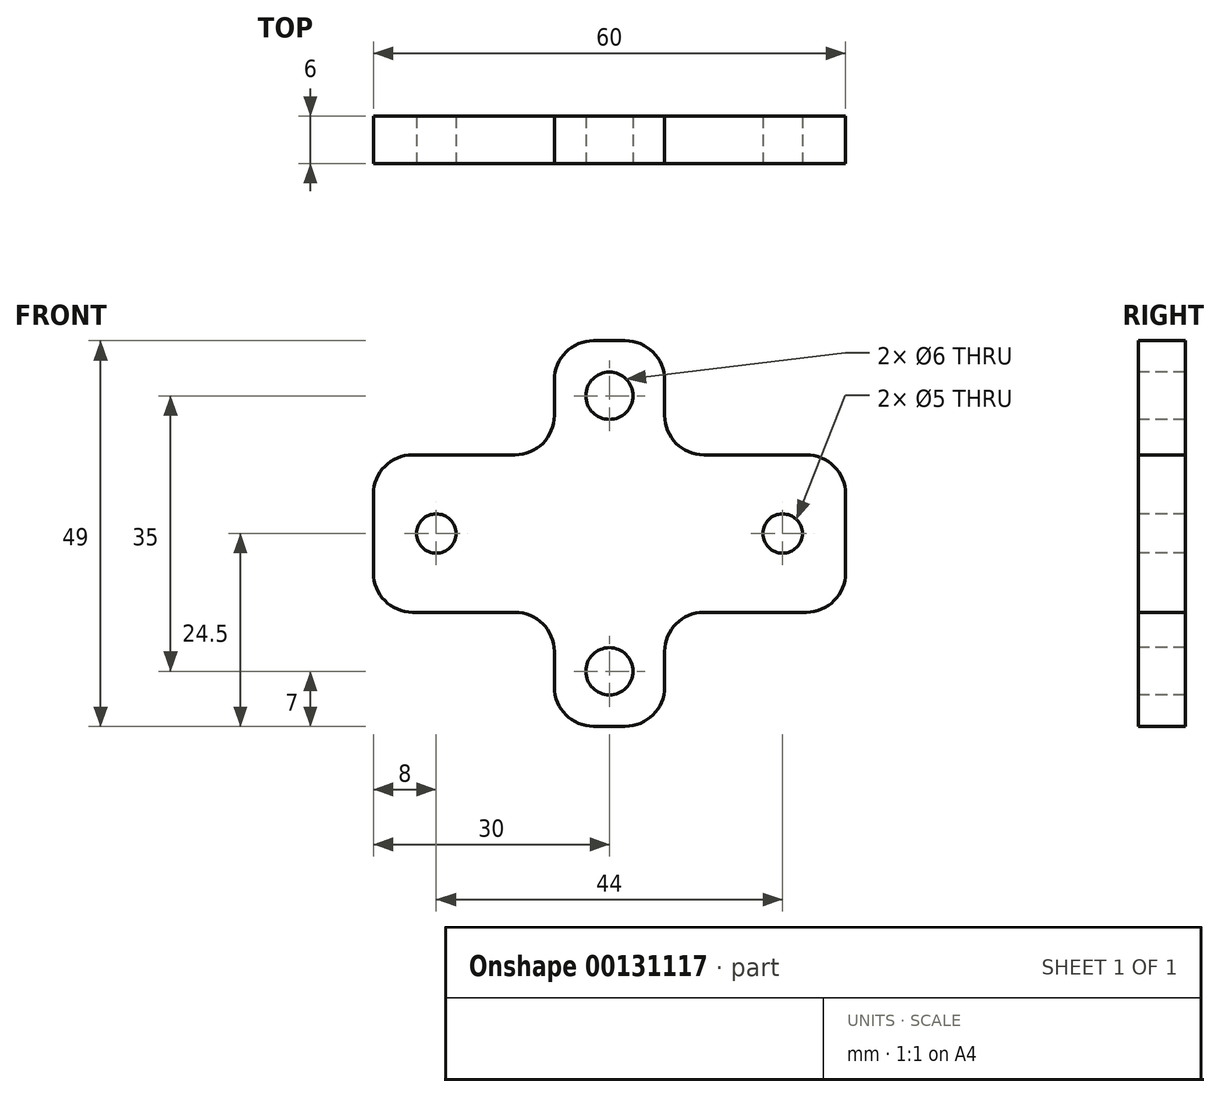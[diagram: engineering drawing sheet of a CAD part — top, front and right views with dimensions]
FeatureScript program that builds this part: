
annotation { "Feature Type Name" : "Feature", "Feature Type Description" : "" }
export const myFeature = defineFeature(function(context is Context, id is Id, definition is map)
    precondition{}
    {
        {
            var Q0;
            Q0=qCreatedBy(makeId("Front.planeOp"),FACE);
            var sketch = newSketch(context, id + "F0", { "sketchPlane" : qUnion([Q0])});
            skLineSegment(sketch, "E0.bottom", {"start": v(7, -24.5) * mm, "end": v(-7, -24.5) * mm});
            skLineSegment(sketch, "E0.top", {"start": v(7, 24.5) * mm, "end": v(-7, 24.5) * mm});
            skLineSegment(sketch, "E0.left", {"start": v(7, -24.5) * mm, "end": v(7, -10) * mm});
            skLineSegment(sketch, "E0.right", {"start": v(-7, -24.5) * mm, "end": v(-7, -10) * mm});
            skPoint(sketch, "E0.middle", {"position": v(0, 0) * mm});
            skPoint(sketch, "E1", {"position": v(0, -17.5) * mm});
            skPoint(sketch, "E2", {"position": v(0, 17.5) * mm});
            skLineSegment(sketch, "E3.bottom", {"start": v(30, -10) * mm, "end": v(7, -10) * mm});
            skLineSegment(sketch, "E3.top", {"start": v(30, 10) * mm, "end": v(7, 10) * mm});
            skLineSegment(sketch, "E3.left", {"start": v(30, -10) * mm, "end": v(30, 10) * mm});
            skLineSegment(sketch, "E3.right", {"start": v(-30, -10) * mm, "end": v(-30, 10) * mm});
            skLineSegment(sketch, "E4.trimOffspring", {"start": v(-7, 10) * mm, "end": v(-7, 24.5) * mm});
            skLineSegment(sketch, "E5.trimOffspring", {"start": v(7, 10) * mm, "end": v(7, 24.5) * mm});
            skLineSegment(sketch, "E6.trimOffspring", {"start": v(-7, -10) * mm, "end": v(-30, -10) * mm});
            skLineSegment(sketch, "E7.trimOffspring", {"start": v(-7, 10) * mm, "end": v(-30, 10) * mm});
            skPoint(sketch, "E8", {"position": v(-22, 0) * mm});
            skPoint(sketch, "E9", {"position": v(22, 0) * mm});
            skSolve(sketch);
        }
        {
            var Q0;
            Q0=makeQuery(id+"F0.imprint","IMPRINT",FACE,{"disambiguationData":[TD([[makeQuery(id+"F0.imprint","IMPRINT",EDGE,{"derivedFrom":sQuery(id+"F0.wireOp",EDGE,"E0.bottom")}),-1.0]])]});
            extrude(context, id + "F1", {"entities" : qUnion([Q0]), "oppositeDirection" : true, "depth" : 6 * mm});
        }
        {
            var Q0;
            Q0=sQuery(id+"F0.wireOp",VERTEX,"E2");
            var Q1;
            Q1=sQuery(id+"F0.wireOp",VERTEX,"E1");
            var Q2;
            Q2=makeQuery(id+"F1.opExtrude","SWEPT_BODY",BODY,{"disambiguationData":[OSD([sQuery(id+"F0.wireOp",EDGE,"E0.bottom"),sQuery(id+"F0.wireOp",EDGE,"E0.top"),sQuery(id+"F0.wireOp",EDGE,"E0.left"),sQuery(id+"F0.wireOp",EDGE,"E0.right"),sQuery(id+"F0.wireOp",EDGE,"E3.bottom"),sQuery(id+"F0.wireOp",EDGE,"E3.top"),sQuery(id+"F0.wireOp",EDGE,"E3.left"),sQuery(id+"F0.wireOp",EDGE,"E3.right"),sQuery(id+"F0.wireOp",EDGE,"E4.trimOffspring"),sQuery(id+"F0.wireOp",EDGE,"E5.trimOffspring"),sQuery(id+"F0.wireOp",EDGE,"E6.trimOffspring"),sQuery(id+"F0.wireOp",EDGE,"E7.trimOffspring")])]});
            hole(context, id + "F2", {"style" : HoleStyle.SIMPLE, "endStyle" : HoleEndStyle.THROUGH, "holeDiameter" : 6 * mm, "locations" : qUnion([Q0, Q1]), "scope" : qUnion([Q2]), "isTappedThrough" : true});
        }
        {
            var Q0;
            Q0=sQuery(id+"F0.wireOp",VERTEX,"E9");
            var Q1;
            Q1=sQuery(id+"F0.wireOp",VERTEX,"E8");
            var Q2;
            Q2=makeQuery(id+"F1.opExtrude","SWEPT_BODY",BODY,{"disambiguationData":[OSD([sQuery(id+"F0.wireOp",EDGE,"E0.bottom"),sQuery(id+"F0.wireOp",EDGE,"E0.top"),sQuery(id+"F0.wireOp",EDGE,"E0.left"),sQuery(id+"F0.wireOp",EDGE,"E0.right"),sQuery(id+"F0.wireOp",EDGE,"E3.bottom"),sQuery(id+"F0.wireOp",EDGE,"E3.top"),sQuery(id+"F0.wireOp",EDGE,"E3.left"),sQuery(id+"F0.wireOp",EDGE,"E3.right"),sQuery(id+"F0.wireOp",EDGE,"E4.trimOffspring"),sQuery(id+"F0.wireOp",EDGE,"E5.trimOffspring"),sQuery(id+"F0.wireOp",EDGE,"E6.trimOffspring"),sQuery(id+"F0.wireOp",EDGE,"E7.trimOffspring")])]});
            hole(context, id + "F3", {"style" : HoleStyle.SIMPLE, "endStyle" : HoleEndStyle.THROUGH, "holeDiameter" : 5 * mm, "locations" : qUnion([Q0, Q1]), "scope" : qUnion([Q2]), "isTappedThrough" : true});
        }
        {
            var Q0;
            Q0=makeQuery(id+"F1.opExtrude","SWEPT_EDGE",EDGE,{"disambiguationData":[OSD([sQuery(id+"F0.wireOp",EDGE,"E0.top"),sQuery(id+"F0.wireOp",EDGE,"E5.trimOffspring")])]});
            var Q1;
            Q1=makeQuery(id+"F1.opExtrude","SWEPT_EDGE",EDGE,{"disambiguationData":[OSD([sQuery(id+"F0.wireOp",EDGE,"E3.top"),sQuery(id+"F0.wireOp",EDGE,"E5.trimOffspring")])]});
            var Q2;
            Q2=makeQuery(id+"F1.opExtrude","SWEPT_EDGE",EDGE,{"disambiguationData":[OSD([sQuery(id+"F0.wireOp",EDGE,"E3.top"),sQuery(id+"F0.wireOp",EDGE,"E3.left")])]});
            var Q3;
            Q3=makeQuery(id+"F1.opExtrude","SWEPT_EDGE",EDGE,{"disambiguationData":[OSD([sQuery(id+"F0.wireOp",EDGE,"E3.bottom"),sQuery(id+"F0.wireOp",EDGE,"E3.left")])]});
            var Q4;
            Q4=makeQuery(id+"F1.opExtrude","SWEPT_EDGE",EDGE,{"disambiguationData":[OSD([sQuery(id+"F0.wireOp",EDGE,"E0.bottom"),sQuery(id+"F0.wireOp",EDGE,"E0.left")])]});
            var Q5;
            Q5=makeQuery(id+"F1.opExtrude","SWEPT_EDGE",EDGE,{"disambiguationData":[OSD([sQuery(id+"F0.wireOp",EDGE,"E0.left"),sQuery(id+"F0.wireOp",EDGE,"E3.bottom")])]});
            var Q6;
            Q6=makeQuery(id+"F1.opExtrude","SWEPT_EDGE",EDGE,{"disambiguationData":[OSD([sQuery(id+"F0.wireOp",EDGE,"E0.bottom"),sQuery(id+"F0.wireOp",EDGE,"E0.right")])]});
            var Q7;
            Q7=makeQuery(id+"F1.opExtrude","SWEPT_EDGE",EDGE,{"disambiguationData":[OSD([sQuery(id+"F0.wireOp",EDGE,"E3.right"),sQuery(id+"F0.wireOp",EDGE,"E6.trimOffspring")])]});
            var Q8;
            Q8=makeQuery(id+"F1.opExtrude","SWEPT_EDGE",EDGE,{"disambiguationData":[OSD([sQuery(id+"F0.wireOp",EDGE,"E0.right"),sQuery(id+"F0.wireOp",EDGE,"E6.trimOffspring")])]});
            var Q9;
            Q9=makeQuery(id+"F1.opExtrude","SWEPT_EDGE",EDGE,{"disambiguationData":[OSD([sQuery(id+"F0.wireOp",EDGE,"E3.right"),sQuery(id+"F0.wireOp",EDGE,"E7.trimOffspring")])]});
            var Q10;
            Q10=makeQuery(id+"F1.opExtrude","SWEPT_EDGE",EDGE,{"disambiguationData":[OSD([sQuery(id+"F0.wireOp",EDGE,"E4.trimOffspring"),sQuery(id+"F0.wireOp",EDGE,"E7.trimOffspring")])]});
            var Q11;
            Q11=makeQuery(id+"F1.opExtrude","SWEPT_EDGE",EDGE,{"disambiguationData":[OSD([sQuery(id+"F0.wireOp",EDGE,"E0.top"),sQuery(id+"F0.wireOp",EDGE,"E4.trimOffspring")])]});
            fillet(context, id + "F4", {"entities" : qUnion([Q0, Q1, Q2, Q3, Q4, Q5, Q6, Q7, Q8, Q9, Q10, Q11]), "radius" : 5 * mm, "tangentPropagation" : true, "allowEdgeOverflow" : false});
        }
    });
